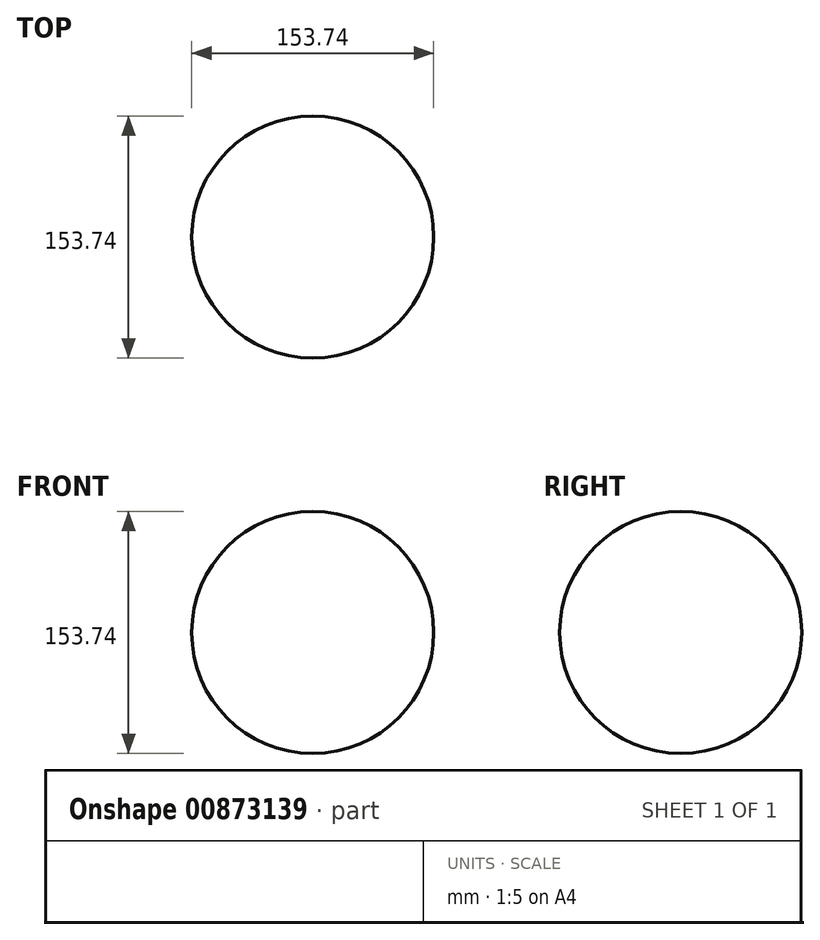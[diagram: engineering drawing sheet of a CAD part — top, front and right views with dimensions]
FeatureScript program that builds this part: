
annotation { "Feature Type Name" : "Feature", "Feature Type Description" : "" }
export const myFeature = defineFeature(function(context is Context, id is Id, definition is map)
    precondition{}
    {
        {
            var Q0;
            Q0=qCreatedBy(makeId("Front.planeOp"),FACE);
            var sketch = newSketch(context, id + "F0", { "sketchPlane" : qUnion([Q0])});
            skArc(sketch, "E0", {"start": v(76.87, 0) * mm, "mid": v(0, 76.87) * mm, "end": v(-76.87, 0) * mm});
            skLineSegment(sketch, "E1", {"start": v(-76.87, 0) * mm, "end": v(76.87, 0) * mm});
            skSolve(sketch);
        }
        {
            var Q0;
            Q0=makeQuery(id+"F0.imprint","IMPRINT",FACE,{"disambiguationData":[TD([[makeQuery(id+"F0.imprint","IMPRINT",EDGE,{"derivedFrom":sQuery(id+"F0.wireOp",EDGE,"E0")}),1.0]])]});
            var Q1;
            Q1=sQuery(id+"F0.wireOp",EDGE,"E1");
            revolve(context, id + "F1", {"surfaceOperationType" : NewSurfaceOperationType.NEW, "entities" : qUnion([Q0]), "axis" : qUnion([Q1]), "revolveType" : RevolveType.FULL});
        }
        {
            var Q0;
            Q0 = qSketchRegion(id + "F0", true);
            var Q1;
            Q1=sQuery(id+"F0.wireOp",EDGE,"E1");
            revolve(context, id + "F2", {"surfaceOperationType" : NewSurfaceOperationType.NEW, "entities" : qUnion([Q0]), "axis" : qUnion([Q1]), "revolveType" : RevolveType.FULL});
        }
    });
